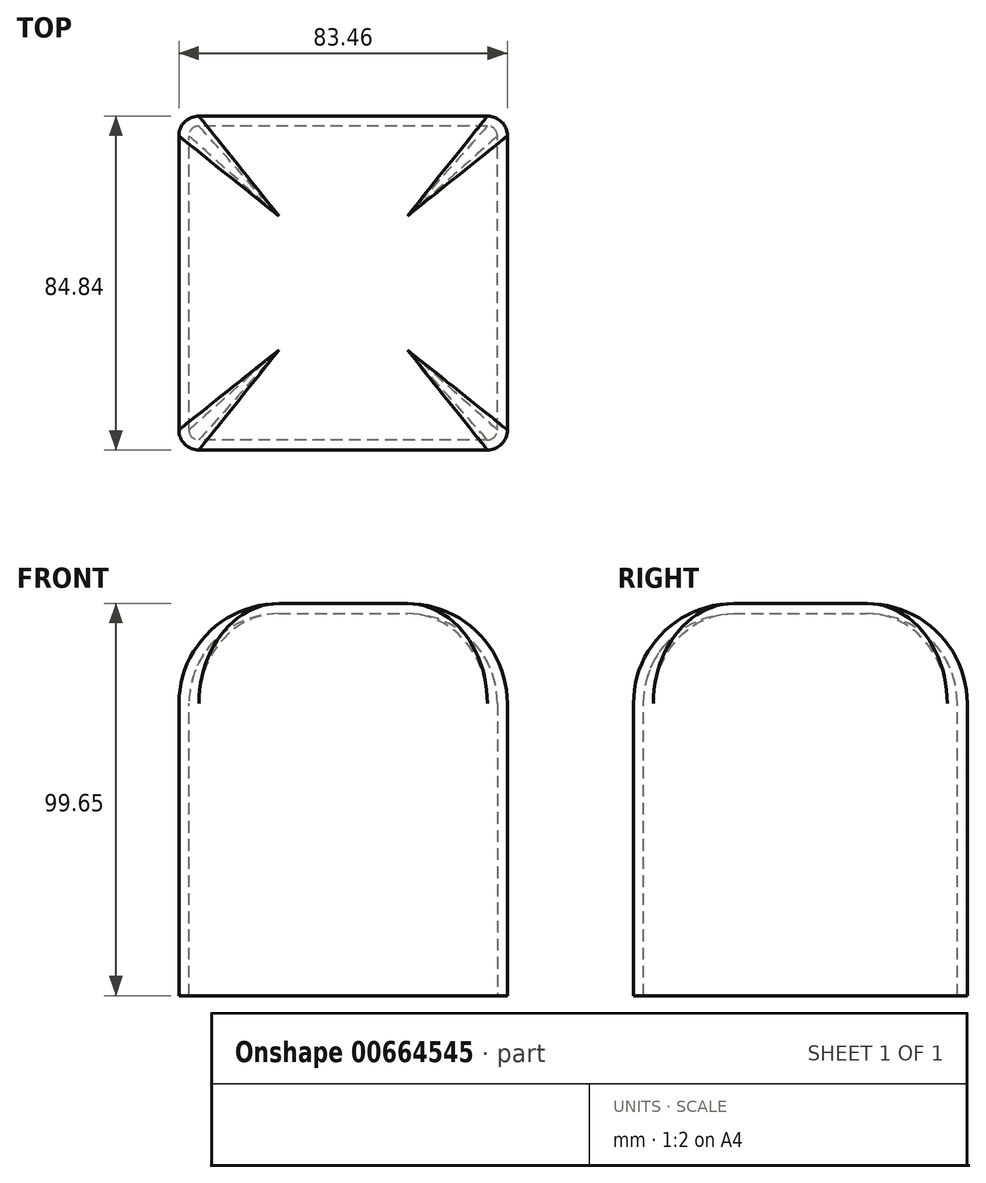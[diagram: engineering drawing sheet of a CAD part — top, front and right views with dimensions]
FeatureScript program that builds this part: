
annotation { "Feature Type Name" : "Feature", "Feature Type Description" : "" }
export const myFeature = defineFeature(function(context is Context, id is Id, definition is map)
    precondition{}
    {
        {
            var Q0;
            Q0=qCreatedBy(makeId("Front.planeOp"),FACE);
            var sketch = newSketch(context, id + "F0", { "sketchPlane" : qUnion([Q0])});
            skLineSegment(sketch, "E0", {"start": v(-47.44, 53.29) * mm, "end": v(36.02, 53.29) * mm});
            skLineSegment(sketch, "E1", {"start": v(36.02, 53.29) * mm, "end": v(36.02, -46.36) * mm});
            skLineSegment(sketch, "E2", {"start": v(36.02, -46.36) * mm, "end": v(-47.44, -46.36) * mm});
            skLineSegment(sketch, "E3", {"start": v(-47.44, -46.36) * mm, "end": v(-47.44, 53.29) * mm});
            skSolve(sketch);
        }
        {
            var Q0;
            Q0=makeQuery(id+"F0.imprint","IMPRINT",FACE,{"disambiguationData":[TD([[makeQuery(id+"F0.imprint","IMPRINT",EDGE,{"derivedFrom":sQuery(id+"F0.wireOp",EDGE,"E0")}),-1.0]])]});
            extrude(context, id + "F1", {"entities" : qUnion([Q0]), "endBound" : BoundingType.SYMMETRIC, "depth" : 84.84 * mm, "offsetDistance" : 25.4 * mm});
        }
        {
            var Q0;
            Q0=makeQuery(id+"F1.opExtrude","CAP_EDGE",EDGE,{"disambiguationData":[OSD([sQuery(id+"F0.wireOp",EDGE,"E0")])],"isStart":false});
            var Q1;
            Q1=makeQuery(id+"F1.opExtrude","SWEPT_EDGE",EDGE,{"disambiguationData":[OSD([sQuery(id+"F0.wireOp",EDGE,"E0"),sQuery(id+"F0.wireOp",EDGE,"E1")])]});
            var Q2;
            Q2=makeQuery(id+"F1.opExtrude","CAP_EDGE",EDGE,{"disambiguationData":[OSD([sQuery(id+"F0.wireOp",EDGE,"E0")])],"isStart":true});
            var Q3;
            Q3=makeQuery(id+"F1.opExtrude","SWEPT_EDGE",EDGE,{"disambiguationData":[OSD([sQuery(id+"F0.wireOp",EDGE,"E0"),sQuery(id+"F0.wireOp",EDGE,"E3")])]});
            var Q4;
            Q4=makeQuery(id+"F1.opExtrude","SWEPT_FACE",FACE,{"disambiguationData":[OSD([sQuery(id+"F0.wireOp",EDGE,"E0")])]});
            fillet(context, id + "F2", {"entities" : qUnion([Q0, Q1, Q2, Q3, Q4]), "radius" : 25.4 * mm, "tangentPropagation" : true, "allowEdgeOverflow" : false});
        }
        {
            var Q0;
            {var subQ0=sQuery(id+"F0.wireOp",EDGE,"E0");Q0=makeQuery(id+"F2.opFillet","BLEND_EDGE",EDGE,{"blendedFrom":[makeQuery(id+"F1.opExtrude","SWEPT_EDGE",EDGE,{"disambiguationData":[OSD([subQ0,sQuery(id+"F0.wireOp",EDGE,"E3")])]}),makeQuery(id+"F1.opExtrude","CAP_EDGE",EDGE,{"disambiguationData":[OSD([subQ0])],"isStart":true})],"blendedInto":[]});}
            var Q1;
            {var subQ0=sQuery(id+"F0.wireOp",EDGE,"E0");Q1=makeQuery(id+"F2.opFillet","BLEND_EDGE",EDGE,{"blendedFrom":[makeQuery(id+"F1.opExtrude","SWEPT_EDGE",EDGE,{"disambiguationData":[OSD([subQ0,sQuery(id+"F0.wireOp",EDGE,"E1")])]}),makeQuery(id+"F1.opExtrude","CAP_EDGE",EDGE,{"disambiguationData":[OSD([subQ0])],"isStart":true})],"blendedInto":[]});}
            var Q2;
            {var subQ0=sQuery(id+"F0.wireOp",EDGE,"E0");Q2=makeQuery(id+"F2.opFillet","BLEND_EDGE",EDGE,{"blendedFrom":[makeQuery(id+"F1.opExtrude","SWEPT_EDGE",EDGE,{"disambiguationData":[OSD([subQ0,sQuery(id+"F0.wireOp",EDGE,"E3")])]}),makeQuery(id+"F1.opExtrude","CAP_EDGE",EDGE,{"disambiguationData":[OSD([subQ0])],"isStart":false})],"blendedInto":[]});}
            var Q3;
            {var subQ0=sQuery(id+"F0.wireOp",EDGE,"E0");Q3=makeQuery(id+"F2.opFillet","BLEND_EDGE",EDGE,{"blendedFrom":[makeQuery(id+"F1.opExtrude","SWEPT_EDGE",EDGE,{"disambiguationData":[OSD([subQ0,sQuery(id+"F0.wireOp",EDGE,"E1")])]}),makeQuery(id+"F1.opExtrude","CAP_EDGE",EDGE,{"disambiguationData":[OSD([subQ0])],"isStart":false})],"blendedInto":[]});}
            fillet(context, id + "F3", {"entities" : qUnion([Q0, Q1, Q2, Q3]), "radius" : 5.08 * mm, "tangentPropagation" : true, "allowEdgeOverflow" : false});
        }
        {
            var Q0;
            Q0=makeQuery(id+"F1.opExtrude","SWEPT_FACE",FACE,{"disambiguationData":[OSD([sQuery(id+"F0.wireOp",EDGE,"E2")])]});
            shell(context, id + "F4", {"entities" : qUnion([Q0]), "thickness" : 2.54 * mm});
        }
    });
